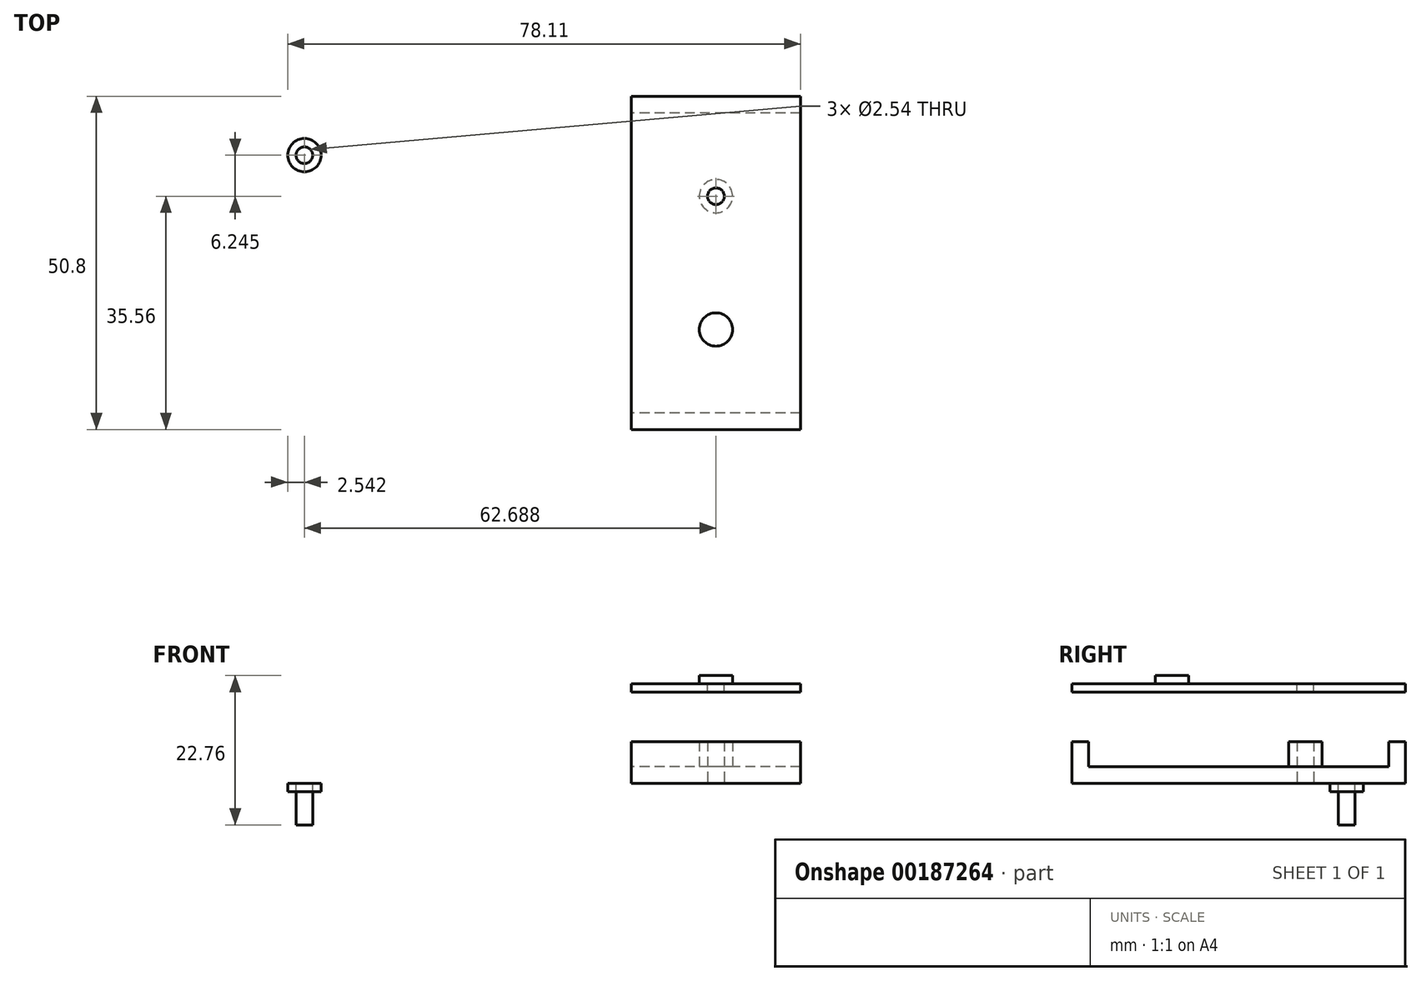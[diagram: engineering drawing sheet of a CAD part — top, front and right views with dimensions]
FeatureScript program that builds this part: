
annotation { "Feature Type Name" : "Feature", "Feature Type Description" : "" }
export const myFeature = defineFeature(function(context is Context, id is Id, definition is map)
    precondition{}
    {
        {
            var Q0;
            Q0=qCreatedBy(makeId("Front.planeOp"),FACE);
            var sketch = newSketch(context, id + "F0", { "sketchPlane" : qUnion([Q0])});
            skLineSegment(sketch, "E0.bottom", {"start": v(-12.88, 2.54) * mm, "end": v(12.88, 2.54) * mm});
            skLineSegment(sketch, "E0.top", {"start": v(-12.88, 0) * mm, "end": v(12.88, 0) * mm});
            skLineSegment(sketch, "E0.left", {"start": v(-12.88, 2.54) * mm, "end": v(-12.88, 0) * mm});
            skLineSegment(sketch, "E0.right", {"start": v(12.88, 2.54) * mm, "end": v(12.88, 0) * mm});
            skPoint(sketch, "E1", {"position": v(0, 0) * mm});
            skLineSegment(sketch, "E2.bottom", {"start": v(-12.88, 2.54) * mm, "end": v(-10.34, 2.54) * mm});
            skLineSegment(sketch, "E2.top", {"start": v(-12.88, 6.35) * mm, "end": v(-10.34, 6.35) * mm});
            skLineSegment(sketch, "E2.left", {"start": v(-12.88, 2.54) * mm, "end": v(-12.88, 6.35) * mm});
            skLineSegment(sketch, "E2.right", {"start": v(-10.34, 2.54) * mm, "end": v(-10.34, 6.35) * mm});
            skLineSegment(sketch, "E3.bottom", {"start": v(12.88, 2.54) * mm, "end": v(10.34, 2.54) * mm});
            skLineSegment(sketch, "E3.top", {"start": v(12.88, 6.35) * mm, "end": v(10.34, 6.35) * mm});
            skLineSegment(sketch, "E3.left", {"start": v(12.88, 2.54) * mm, "end": v(12.88, 6.35) * mm});
            skLineSegment(sketch, "E3.right", {"start": v(10.34, 2.54) * mm, "end": v(10.34, 6.35) * mm});
            skSolve(sketch);
        }
        {
            var Q0;
            Q0=makeQuery(id+"F0.imprint","IMPRINT",FACE,{"disambiguationData":[TD([[makeQuery(id+"F0.imprint","IMPRINT",EDGE,{"derivedFrom":sQuery(id+"F0.wireOp",EDGE,"E0.bottom")}),-1.0]])]});
            var Q1;
            Q1=makeQuery(id+"F0.imprint","IMPRINT",FACE,{"disambiguationData":[TD([[makeQuery(id+"F0.imprint","IMPRINT",EDGE,{"derivedFrom":sQuery(id+"F0.wireOp",EDGE,"E2.bottom")}),1.0]])]});
            var Q2;
            Q2=makeQuery(id+"F0.imprint","IMPRINT",FACE,{"disambiguationData":[TD([[makeQuery(id+"F0.imprint","IMPRINT",EDGE,{"derivedFrom":sQuery(id+"F0.wireOp",EDGE,"E3.bottom")}),-1.0]])]});
            extrude(context, id + "F1", {"entities" : qUnion([Q0, Q1, Q2]), "endBound" : BoundingType.SYMMETRIC, "depth" : 50.8 * mm});
        }
        {
            var Q0;
            Q0=qCreatedBy(makeId("Top.planeOp"),FACE);
            var sketch = newSketch(context, id + "F2", { "sketchPlane" : qUnion([Q0])});
            skLineSegment(sketch, "E4.bottom", {"start": v(-12.88, -25.4) * mm, "end": v(12.88, -25.4) * mm});
            skLineSegment(sketch, "E4.top", {"start": v(-12.88, -22.86) * mm, "end": v(12.88, -22.86) * mm});
            skLineSegment(sketch, "E4.left", {"start": v(-12.88, -25.4) * mm, "end": v(-12.88, -22.86) * mm});
            skLineSegment(sketch, "E4.right", {"start": v(12.88, -25.4) * mm, "end": v(12.88, -22.86) * mm});
            skLineSegment(sketch, "E5.bottom", {"start": v(-12.88, 25.4) * mm, "end": v(12.88, 25.4) * mm});
            skLineSegment(sketch, "E5.top", {"start": v(-12.88, 22.86) * mm, "end": v(12.88, 22.86) * mm});
            skLineSegment(sketch, "E5.left", {"start": v(-12.88, 25.4) * mm, "end": v(-12.88, 22.86) * mm});
            skLineSegment(sketch, "E5.right", {"start": v(12.88, 25.4) * mm, "end": v(12.88, 22.86) * mm});
            skSolve(sketch);
        }
        {
            var Q0;
            Q0=makeQuery(id+"F2.imprint","IMPRINT",FACE,{"disambiguationData":[TD([[makeQuery(id+"F2.imprint","IMPRINT",EDGE,{"derivedFrom":sQuery(id+"F2.wireOp",EDGE,"E4.bottom")}),1.0]])]});
            var Q1;
            Q1=makeQuery(id+"F2.imprint","IMPRINT",FACE,{"disambiguationData":[TD([[makeQuery(id+"F2.imprint","IMPRINT",EDGE,{"derivedFrom":sQuery(id+"F2.wireOp",EDGE,"E5.bottom")}),-1.0]])]});
            extrude(context, id + "F3", {"entities" : qUnion([Q0, Q1]), "operationType" : NewBodyOperationType.ADD, "depth" : 6.35 * mm});
        }
        {
            var Q0;
            Q0=qCreatedBy(makeId("Top.planeOp"),FACE);
            var sketch = newSketch(context, id + "F4", { "sketchPlane" : qUnion([Q0])});
            skLineSegment(sketch, "E6", {"start": v(0, 0) * mm, "end": v(0, 10.16) * mm});
            skCircle(sketch, "E7", {"center": v(0, 10.16) * mm, "radius": 2.54 * mm});
            skCircle(sketch, "E8.0", {"center": v(0, 10.16) * mm, "radius": 1.27 * mm});
            skCircle(sketch, "E9.MirrorC", {"center": v(0, -10.16) * mm, "radius": 2.54 * mm});
            skCircle(sketch, "E10.MirrorC", {"center": v(0, -10.16) * mm, "radius": 1.27 * mm});
            skSolve(sketch);
        }
        {
            var Q0;
            Q0=makeQuery(id+"F4.imprint","IMPRINT",FACE,{"disambiguationData":[TD([[makeQuery(id+"F4.imprint","IMPRINT",EDGE,{"derivedFrom":sQuery(id+"F4.wireOp",EDGE,"E9.MirrorC")}),-1.0]])]});
            var Q1;
            Q1=makeQuery(id+"F4.imprint","IMPRINT",FACE,{"disambiguationData":[TD([[makeQuery(id+"F4.imprint","IMPRINT",EDGE,{"derivedFrom":sQuery(id+"F4.wireOp",EDGE,"E7")}),1.0]])]});
            extrude(context, id + "F5", {"entities" : qUnion([Q0, Q1]), "operationType" : NewBodyOperationType.ADD, "depth" : 6.35 * mm});
        }
        {
            var Q0;
            Q0=qCreatedBy(makeId("Right.planeOp"),FACE);
            var sketch = newSketch(context, id + "F6", { "sketchPlane" : qUnion([Q0])});
            skLineSegment(sketch, "E11.bottom", {"start": v(-25.4, 13.87) * mm, "end": v(25.4, 13.87) * mm});
            skLineSegment(sketch, "E11.top", {"start": v(-25.4, 16.4) * mm, "end": v(25.4, 16.4) * mm});
            skLineSegment(sketch, "E11.left", {"start": v(-25.4, 13.87) * mm, "end": v(-25.4, 16.4) * mm});
            skLineSegment(sketch, "E11.right", {"start": v(25.4, 13.87) * mm, "end": v(25.4, 16.4) * mm});
            skSolve(sketch);
        }
        {
            var Q0;
            Q0=makeQuery(id+"F6.imprint","IMPRINT",FACE,{"disambiguationData":[TD([[makeQuery(id+"F6.imprint","IMPRINT",EDGE,{"derivedFrom":sQuery(id+"F6.wireOp",EDGE,"E11.bottom")}),1.0]])]});
            extrude(context, id + "F7", {"entities" : qUnion([Q0]), "endBound" : BoundingType.SYMMETRIC, "depth" : 25.76 * mm});
        }
        {
            var Q0;
            Q0=makeQuery(id+"F7.opExtrude","SWEPT_FACE",FACE,{"disambiguationData":[OSD([sQuery(id+"F6.wireOp",EDGE,"E11.top")])]});
            var sketch = newSketch(context, id + "F8", { "sketchPlane" : qUnion([Q0])});
            skCircle(sketch, "E12", {"center": v(0, 10.16) * mm, "radius": 2.54 * mm});
            skCircle(sketch, "E13.0", {"center": v(0, 10.16) * mm, "radius": 1.27 * mm});
            skCircle(sketch, "E14.MirrorC", {"center": v(0, -10.16) * mm, "radius": 2.54 * mm});
            skCircle(sketch, "E15.MirrorC", {"center": v(0, -10.16) * mm, "radius": 1.27 * mm});
            skSolve(sketch);
        }
        {
            var Q0;
            Q0=makeQuery(id+"F8.imprint","IMPRINT",FACE,{"disambiguationData":[TD([[makeQuery(id+"F8.imprint","IMPRINT",EDGE,{"derivedFrom":sQuery(id+"F8.wireOp",EDGE,"E14.MirrorC")}),-1.0]])]});
            var Q1;
            Q1=makeQuery(id+"F8.imprint","IMPRINT",FACE,{"disambiguationData":[TD([[makeQuery(id+"F8.imprint","IMPRINT",EDGE,{"derivedFrom":sQuery(id+"F8.wireOp",EDGE,"E12")}),1.0]])]});
            extrude(context, id + "F9", {"entities" : qUnion([Q0, Q1]), "operationType" : NewBodyOperationType.REMOVE, "oppositeDirection" : true, "depth" : 1.27 * mm});
        }
        {
            var Q0;
            Q0=makeQuery(id+"F9.boolean.opBoolean","SPLIT",FACE,{"disambiguationData":[TD([makeQuery(id+"F9.opExtrude","SWEPT_FACE",FACE,{"disambiguationData":[OSD([sQuery(id+"F8.wireOp",EDGE,"E15.MirrorC")])]})])],"derivedFrom":makeQuery(id+"F7.opExtrude","SWEPT_FACE",FACE,{"disambiguationData":[OSD([sQuery(id+"F6.wireOp",EDGE,"E11.top")])]})});
            var Q1;
            Q1=makeQuery(id+"F9.boolean.opBoolean","SPLIT",FACE,{"disambiguationData":[TD([makeQuery(id+"F9.opExtrude","SWEPT_FACE",FACE,{"disambiguationData":[OSD([sQuery(id+"F8.wireOp",EDGE,"E13.0")])]})])],"derivedFrom":makeQuery(id+"F7.opExtrude","SWEPT_FACE",FACE,{"disambiguationData":[OSD([sQuery(id+"F6.wireOp",EDGE,"E11.top")])]})});
            extrude(context, id + "F10", {"entities" : qUnion([Q0, Q1]), "operationType" : NewBodyOperationType.REMOVE, "oppositeDirection" : true, "depth" : 25.4 * mm});
        }
        {
            var Q0;
            Q0=qCreatedBy(makeId("Top.planeOp"),FACE);
            var sketch = newSketch(context, id + "F11", { "sketchPlane" : qUnion([Q0])});
            skCircle(sketch, "E16", {"center": v(-62.69, 16.4) * mm, "radius": 2.54 * mm});
            skCircle(sketch, "E17.0", {"center": v(-62.69, 16.4) * mm, "radius": 1.27 * mm});
            skSolve(sketch);
        }
        {
            var Q0;
            Q0=makeQuery(id+"F11.imprint","IMPRINT",FACE,{"disambiguationData":[TD([[makeQuery(id+"F11.imprint","IMPRINT",EDGE,{"derivedFrom":sQuery(id+"F11.wireOp",EDGE,"E16")}),1.0]])]});
            extrude(context, id + "F12", {"entities" : qUnion([Q0]), "oppositeDirection" : true, "depth" : 1.27 * mm});
        }
        {
            var Q0;
            Q0=makeQuery(id+"F11.imprint","IMPRINT",FACE,{"disambiguationData":[TD([[makeQuery(id+"F11.imprint","IMPRINT",EDGE,{"derivedFrom":sQuery(id+"F11.wireOp",EDGE,"E17.0")}),1.0]])]});
            extrude(context, id + "F13", {"entities" : qUnion([Q0]), "oppositeDirection" : true, "depth" : 6.35 * mm});
        }
    });
